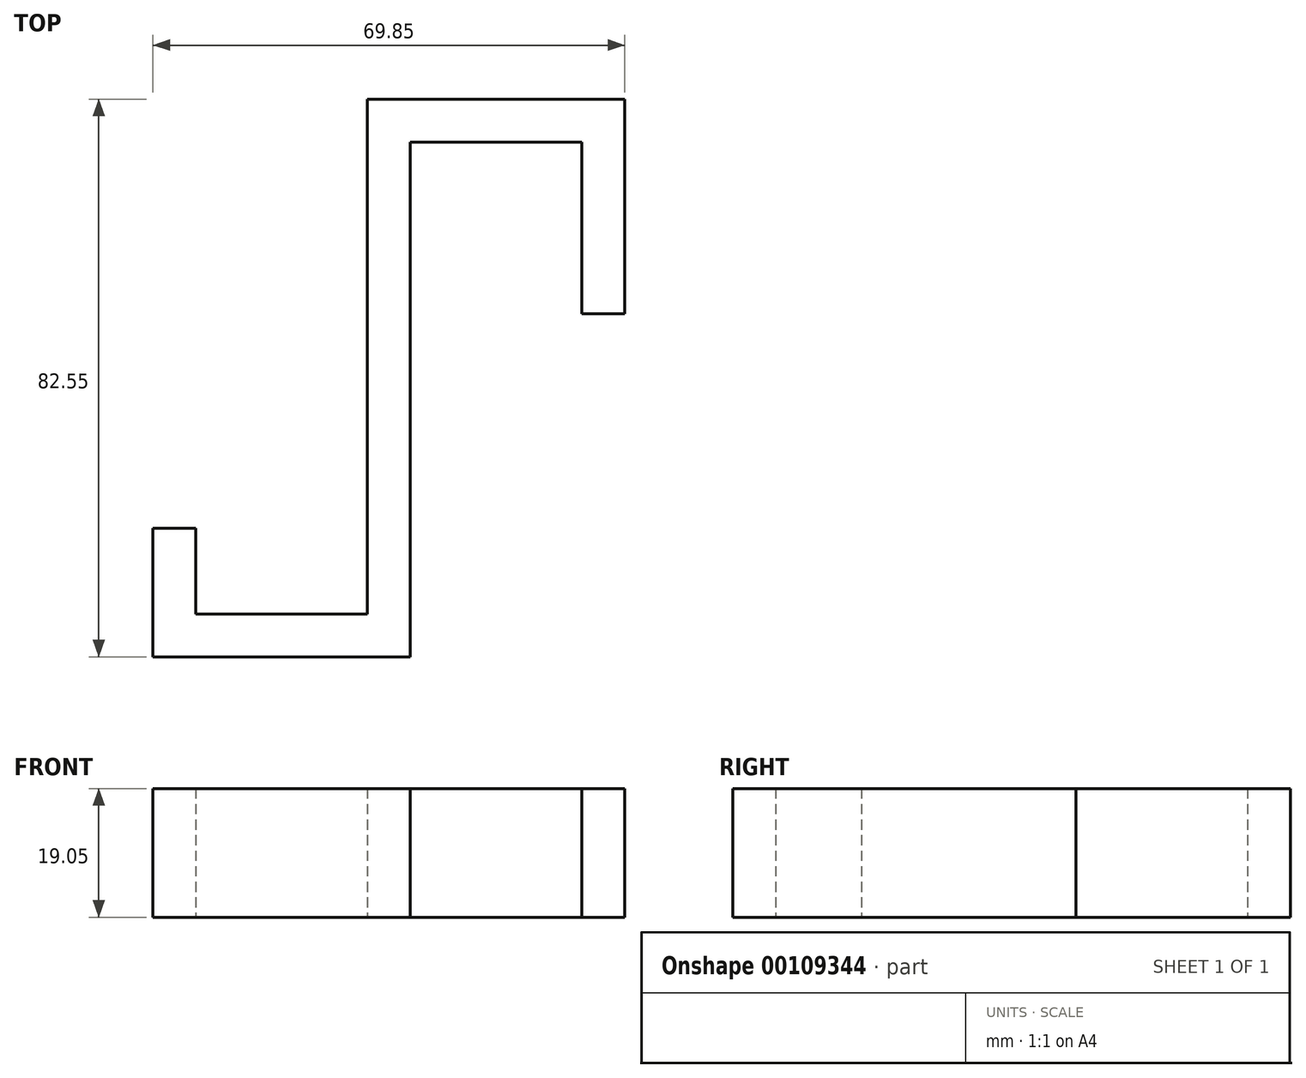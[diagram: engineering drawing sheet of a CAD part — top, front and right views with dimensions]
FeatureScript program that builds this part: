
annotation { "Feature Type Name" : "Feature", "Feature Type Description" : "" }
export const myFeature = defineFeature(function(context is Context, id is Id, definition is map)
    precondition{}
    {
        {
            var Q0;
            Q0=qCreatedBy(makeId("Top.planeOp"),FACE);
            var sketch = newSketch(context, id + "F0", { "sketchPlane" : qUnion([Q0])});
            skLineSegment(sketch, "E0", {"start": v(-47.48, -30.7) * mm, "end": v(-22.08, -30.7) * mm});
            skLineSegment(sketch, "E1", {"start": v(-22.08, -30.7) * mm, "end": v(-22.08, 45.5) * mm});
            skLineSegment(sketch, "E2", {"start": v(-22.08, 45.5) * mm, "end": v(16.02, 45.5) * mm});
            skLineSegment(sketch, "E3", {"start": v(16.02, 45.5) * mm, "end": v(16.02, 13.76) * mm});
            skLineSegment(sketch, "E4", {"start": v(16.02, 13.76) * mm, "end": v(9.67, 13.76) * mm});
            skLineSegment(sketch, "E5", {"start": v(9.67, 13.76) * mm, "end": v(9.67, 39.16) * mm});
            skLineSegment(sketch, "E6", {"start": v(9.67, 39.16) * mm, "end": v(-15.73, 39.16) * mm});
            skLineSegment(sketch, "E7", {"start": v(-15.73, 39.16) * mm, "end": v(-15.73, -37.04) * mm});
            skLineSegment(sketch, "E8", {"start": v(-15.73, -37.04) * mm, "end": v(-53.83, -37.04) * mm});
            skLineSegment(sketch, "E9", {"start": v(-53.83, -37.04) * mm, "end": v(-53.83, -18) * mm});
            skLineSegment(sketch, "E10", {"start": v(-53.83, -18) * mm, "end": v(-47.48, -18) * mm});
            skLineSegment(sketch, "E11", {"start": v(-47.48, -18) * mm, "end": v(-47.48, -30.7) * mm});
            skLineSegment(sketch, "E12", {"start": v(-22.08, 11.5) * mm, "end": v(-15.73, 11.5) * mm, "construction": true});
            skLineSegment(sketch, "E13", {"start": v(6.46, 39.16) * mm, "end": v(6.46, 45.5) * mm, "construction": true});
            skLineSegment(sketch, "E14", {"start": v(-34.78, -30.7) * mm, "end": v(-34.78, -37.04) * mm, "construction": true});
            skSolve(sketch);
        }
        {
            var Q0;
            Q0 = qSketchRegion(id + "F0", true);
            extrude(context, id + "F1", {"entities" : qUnion([Q0]), "depth" : 19.05 * mm});
        }
    });
